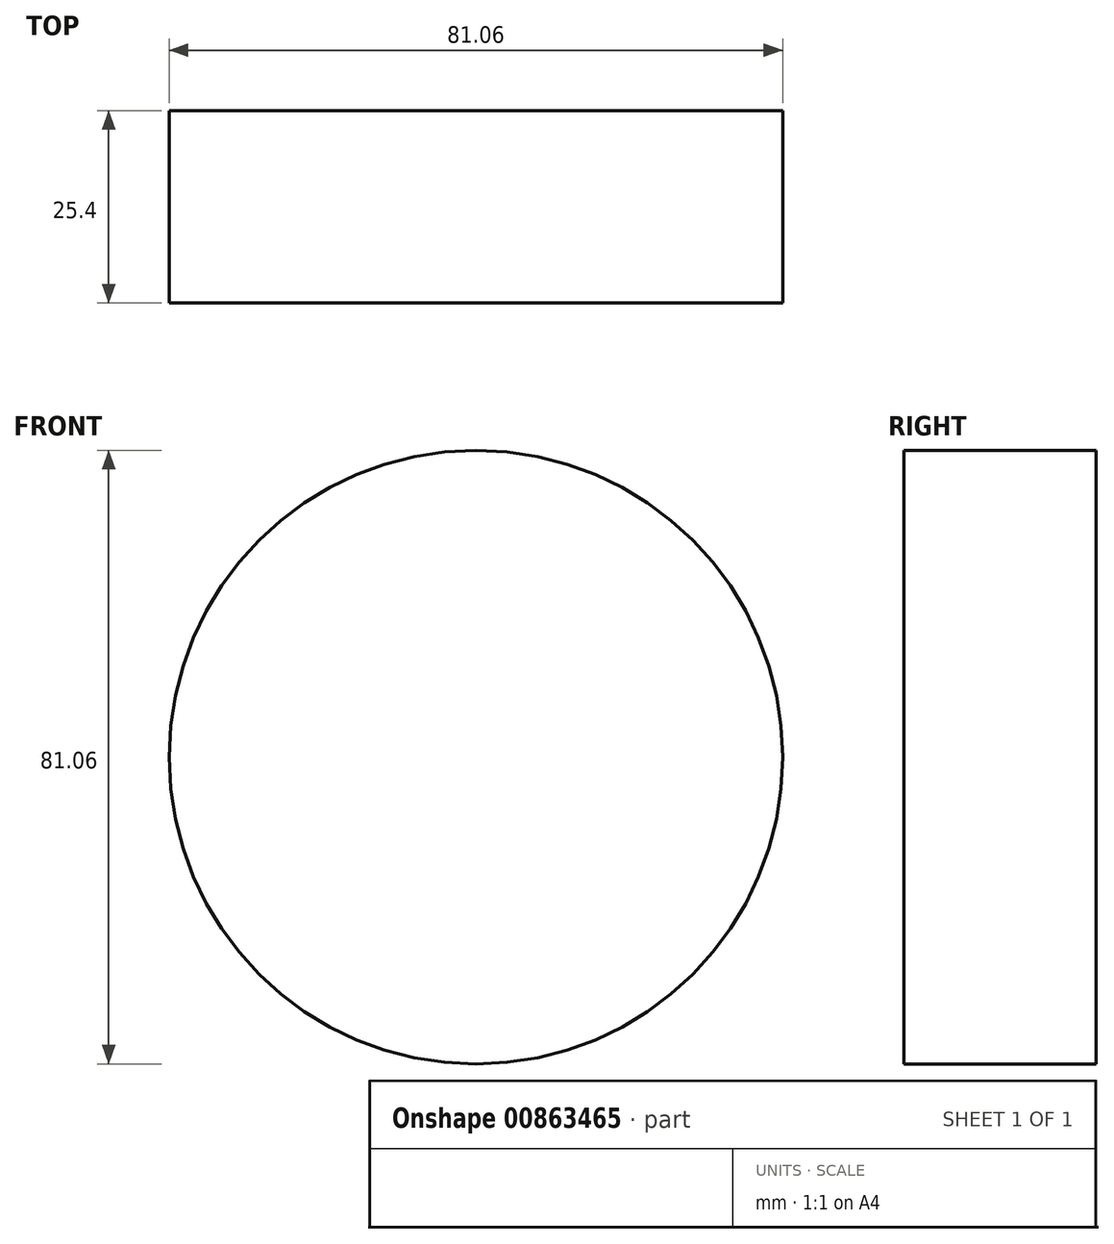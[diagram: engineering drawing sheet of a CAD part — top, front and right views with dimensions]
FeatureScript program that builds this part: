
annotation { "Feature Type Name" : "Feature", "Feature Type Description" : "" }
export const myFeature = defineFeature(function(context is Context, id is Id, definition is map)
    precondition{}
    {
        {
            var Q0;
            Q0=qCreatedBy(makeId("Front.planeOp"),FACE);
            var sketch = newSketch(context, id + "F0", { "sketchPlane" : qUnion([Q0])});
            skCircle(sketch, "E0", {"center": v(0, 0) * mm, "radius": 40.53 * mm});
            skSolve(sketch);
        }
        {
            var Q0;
            Q0 = qSketchRegion(id + "F0", true);
            extrude(context, id + "F1", {"entities" : qUnion([Q0]), "depth" : 25.4 * mm, "offsetDistance" : 25.4 * mm});
        }
    });
